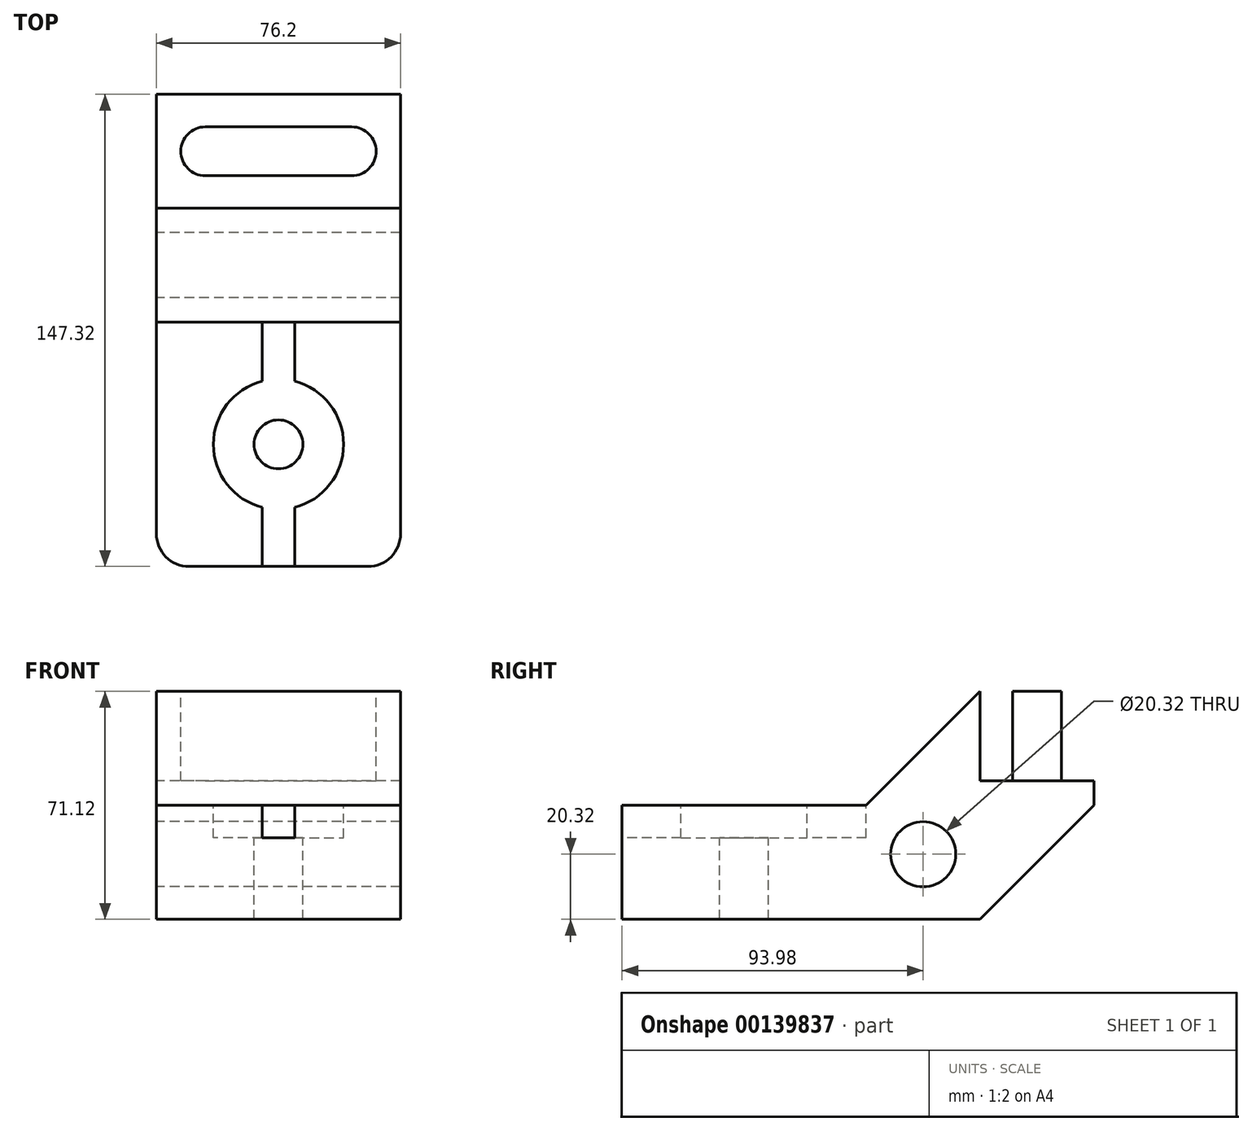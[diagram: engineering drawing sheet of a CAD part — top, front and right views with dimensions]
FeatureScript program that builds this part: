
annotation { "Feature Type Name" : "Feature", "Feature Type Description" : "" }
export const myFeature = defineFeature(function(context is Context, id is Id, definition is map)
    precondition{}
    {
        {
            var Q0;
            Q0=qCreatedBy(makeId("Right.planeOp"),FACE);
            var sketch = newSketch(context, id + "F0", { "sketchPlane" : qUnion([Q0])});
            skLineSegment(sketch, "E0", {"start": v(0, 0) * mm, "end": v(0, 35.56) * mm});
            skLineSegment(sketch, "E1", {"start": v(0, 35.56) * mm, "end": v(76.2, 35.56) * mm});
            skLineSegment(sketch, "E2", {"start": v(76.2, 35.56) * mm, "end": v(111.76, 71.12) * mm});
            skLineSegment(sketch, "E3", {"start": v(111.76, 71.12) * mm, "end": v(147.32, 71.12) * mm});
            skLineSegment(sketch, "E4", {"start": v(147.32, 71.12) * mm, "end": v(147.32, 35.56) * mm});
            skLineSegment(sketch, "E5", {"start": v(147.32, 35.56) * mm, "end": v(111.76, 0) * mm});
            skLineSegment(sketch, "E6", {"start": v(111.76, 0) * mm, "end": v(0, 0) * mm});
            skCircle(sketch, "E7", {"center": v(93.98, 20.32) * mm, "radius": 10.16 * mm});
            skSolve(sketch);
        }
        {
            var Q0;
            Q0 = qSketchRegion(id + "F0", true);
            extrude(context, id + "F1", {"entities" : qUnion([Q0]), "depth" : 76.2 * mm});
        }
        {
            var Q0;
            Q0=makeQuery(id+"F1.opExtrude","SWEPT_FACE",FACE,{"disambiguationData":[OSD([sQuery(id+"F0.wireOp",EDGE,"E3")])]});
            var sketch = newSketch(context, id + "F2", { "sketchPlane" : qUnion([Q0])});
            skLineSegment(sketch, "E8.0", {"start": v(76.2, 147.32) * mm, "end": v(0, 147.32) * mm});
            skLineSegment(sketch, "E9.0", {"start": v(76.2, 111.76) * mm, "end": v(76.2, 147.32) * mm});
            skLineSegment(sketch, "E10.0", {"start": v(76.2, 111.76) * mm, "end": v(0, 111.76) * mm});
            skLineSegment(sketch, "E11.0", {"start": v(0, 111.76) * mm, "end": v(0, 147.32) * mm});
            skLineSegment(sketch, "E12", {"start": v(15.24, 129.54) * mm, "end": v(60.96, 129.54) * mm});
            skArc(sketch, "E13.0.startCap", {"start": v(15.24, 121.92) * mm, "mid": v(7.62, 129.54) * mm, "end": v(15.24, 137.16) * mm});
            skArc(sketch, "E13.0.endCap", {"start": v(60.96, 137.16) * mm, "mid": v(68.58, 129.54) * mm, "end": v(60.96, 121.92) * mm});
            skLineSegment(sketch, "E13.0.left", {"start": v(15.24, 137.16) * mm, "end": v(60.96, 137.16) * mm});
            skLineSegment(sketch, "E13.0.right", {"start": v(15.24, 121.92) * mm, "end": v(60.96, 121.92) * mm});
            skSolve(sketch);
        }
        {
            var Q0;
            Q0=makeQuery(id+"F2.imprint","IMPRINT",FACE,{"disambiguationData":[TD([[makeQuery(id+"F2.imprint","IMPRINT",EDGE,{"derivedFrom":sQuery(id+"F2.wireOp",EDGE,"E13.0.startCap")}),-1.0]])]});
            extrude(context, id + "F3", {"entities" : qUnion([Q0]), "operationType" : NewBodyOperationType.REMOVE, "oppositeDirection" : true, "depth" : 27.94 * mm});
        }
        {
            var Q0;
            Q0=makeQuery(id+"F1.opExtrude","CAP_EDGE",EDGE,{"disambiguationData":[OSD([sQuery(id+"F0.wireOp",EDGE,"E0")])],"isStart":false});
            var Q1;
            Q1=makeQuery(id+"F1.opExtrude","CAP_EDGE",EDGE,{"disambiguationData":[OSD([sQuery(id+"F0.wireOp",EDGE,"E0")])],"isStart":true});
            fillet(context, id + "F4", {"entities" : qUnion([Q0, Q1]), "radius" : 10.16 * mm, "tangentPropagation" : true, "allowEdgeOverflow" : false});
        }
        {
            var Q0;
            Q0=makeQuery(id+"F1.opExtrude","SWEPT_FACE",FACE,{"disambiguationData":[OSD([sQuery(id+"F0.wireOp",EDGE,"E1")])]});
            var sketch = newSketch(context, id + "F5", { "sketchPlane" : qUnion([Q0])});
            skLineSegment(sketch, "E14", {"start": v(38.1, 76.2) * mm, "end": v(38.1, 0) * mm, "construction": true});
            skLineSegment(sketch, "E15.0", {"start": v(43.18, 76.2) * mm, "end": v(43.18, 0) * mm});
            skLineSegment(sketch, "E16.MirrorCS", {"start": v(33.02, 76.2) * mm, "end": v(33.02, 0) * mm});
            skLineSegment(sketch, "E17", {"start": v(33.02, 76.2) * mm, "end": v(43.18, 76.2) * mm});
            skLineSegment(sketch, "E18", {"start": v(43.18, 0) * mm, "end": v(33.02, 0) * mm});
            skPoint(sketch, "E19", {"position": v(38.1, 38.1) * mm});
            skSolve(sketch);
        }
        {
            var Q0;
            Q0=sQuery(id+"F5.wireOp",VERTEX,"E19");
            var Q1;
            Q1=makeQuery(id+"F1.opExtrude","SWEPT_BODY",BODY,{"disambiguationData":[OSD([sQuery(id+"F0.wireOp",EDGE,"E0"),sQuery(id+"F0.wireOp",EDGE,"E1"),sQuery(id+"F0.wireOp",EDGE,"E2"),sQuery(id+"F0.wireOp",EDGE,"E3"),sQuery(id+"F0.wireOp",EDGE,"E4"),sQuery(id+"F0.wireOp",EDGE,"E5"),sQuery(id+"F0.wireOp",EDGE,"E6"),sQuery(id+"F0.wireOp",EDGE,"E7")])]});
            hole(context, id + "F6", {"style" : HoleStyle.C_BORE, "endStyle" : HoleEndStyle.THROUGH, "holeDiameter" : 15.24 * mm, "cBoreDiameter" : 40.64 * mm, "cBoreDepth" : 10.16 * mm, "locations" : qUnion([Q0]), "scope" : qUnion([Q1]), "isTappedThrough" : true});
        }
        {
            var Q0;
            Q0 = qSketchRegion(id + "F5", true);
            extrude(context, id + "F7", {"entities" : qUnion([Q0]), "operationType" : NewBodyOperationType.REMOVE, "oppositeDirection" : true, "depth" : 10.16 * mm});
        }
    });
